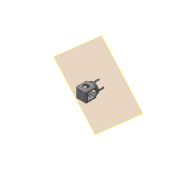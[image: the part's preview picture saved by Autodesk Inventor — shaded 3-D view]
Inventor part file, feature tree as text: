
AUTODESK INVENTOR PART (.ipt)
format: ipt  version: 2017 (Build 210142000, 142)  size: 828,928 bytes
history: native  units: in
note: dims shown in document units (in); Inventor stores cm internally (conversion verified against a paired STEP export)
features: fillet x10, sketch x9, extrude x9, projected_geometry x6, other x4, reference x3, plane x2
ambient origin geometry x8: Origin, YZ Plane, XZ Plane, XY Plane, X Axis, Y Axis, Z Axis, Center Point
bodies: Solid1 (feature_tree)
feature tree (43):
  plane  "Work Plane1"
  sketch  "Sketch1"  dims[d0=0.0in d1=0.0in]
  plane  "Work Plane2"
  extrude  "Extrusion1"  TaperAngle=0.0deg  [1 undecoded]
  extrude  "Extrusion2"  Depth=0.0625in
  extrude  "Extrusion3"  Depth=1.0in TaperAngle=0.0deg
  extrude  "Extrusion4"  Depth=0.3in TaperAngle=0.0deg
  extrude  "Extrusion5"  TaperAngle=0.0deg  [1 undecoded]
  extrude  "Extrusion6"  Depth=1.0in TaperAngle=0.0deg
  extrude  "Extrusion7"  Depth=1.0in TaperAngle=0.0deg
  fillet  "Fillet1"  Radius=0.01in
  fillet  "Fillet2"  Radius=0.0625in
  fillet  "Fillet3"  Radius=0.125in
  fillet  "Fillet4"  Radius=0.125in
  extrude  "Extrusion8"  Depth=0.04in
  fillet  "Fillet5"  Radius=0.0625in
  fillet  "Fillet6"  Radius=0.0625in
  fillet  "Fillet7"  Radius=0.0625in
  fillet  "Fillet8"  Radius=0.0625in
  fillet  "Fillet9"  Radius=0.5in
  extrude  "Extrusion9"  Depth=0.0325in
  fillet  "Fillet10"  Radius=0.035in
  reference  "Reference1"
  sketch  "Sketch2"  dims[d2=0.0625in d3=0.0625in]
  projected_geometry  "Projected Loop1"
  reference  "Reference2"
  sketch  "Sketch3"  dims[d4=0.01in d5=1.0in d6=0.0in]
  projected_geometry  "Projected Loop2"
  sketch  "Sketch4"  dims[d7=0.0625in d8=0.0in d9=0.3in d10=0.0in]
  sketch  "Sketch5"  dims[d11=0.0in d12=0.0in]
  projected_geometry  "Projected Loop3"
  sketch  "Sketch6"  dims[d13=1.0in d14=1.0in d15=0.0in]
  projected_geometry  "Projected Loop4"
  sketch  "Sketch7"  dims[d16=0.4626in d17=1.0in d18=0.0in d19=0.01in d20=0.0in d21=0.0625in d22=0.0in d23=0.125in d24=0.125in]
  projected_geometry  "Projected Loop5"
  reference  "Reference3"
  sketch  "Sketch8"  dims[d25=0.125in d26=0.04in d27=0.0625in d28=0.0625in d29=0.0625in d30=0.0625in d31=0.5in d32=0.0in]
  sketch  "Sketch9"  dims[d33=0.05in d34=0.035in d35=0.035in d36=0.035in d37=0.035in d38=2.0in d39=0.0in d40=0.0325in]
  projected_geometry  "Projected Loop6"
  parser-record x1  (decoder bookkeeping rows leaked as tree rows — omitted from the tree; the rows remain in map.json)
  other  "p1.iam"
  other  "bearing_1:1"
  other  "teststand:1"
note: 2 required parameter values undecoded (feature->parameter linkage not recoverable at this tier; creation-order binding heuristic only, values carry confidence <= 0.55)
note: 1 file-system path scrubbed to <path> (originals preserved in map.json)
